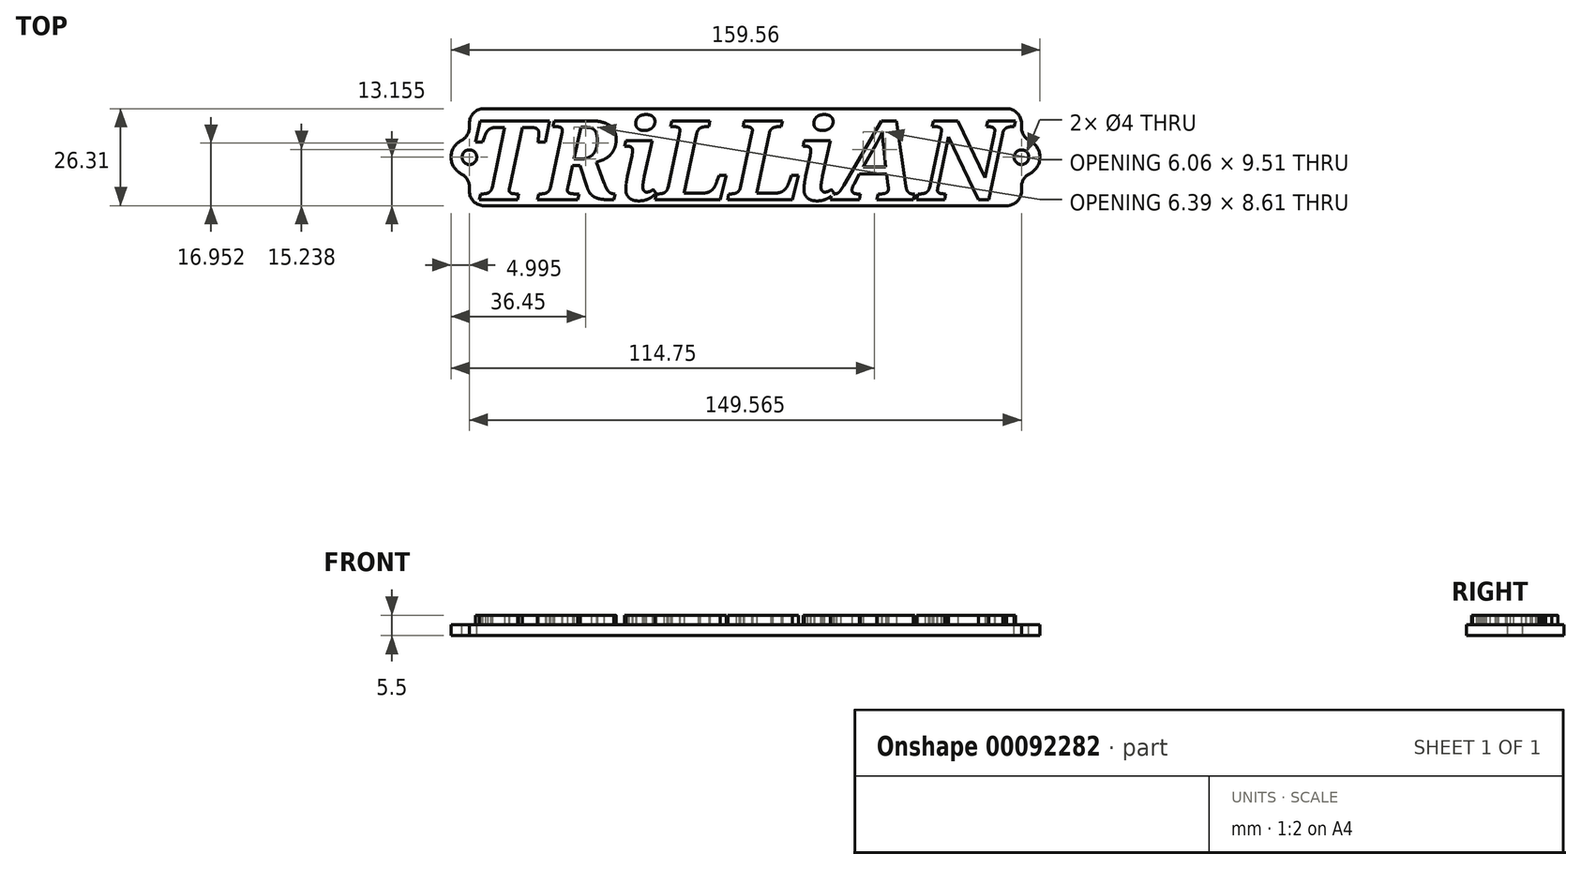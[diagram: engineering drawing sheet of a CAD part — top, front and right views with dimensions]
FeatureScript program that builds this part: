
annotation { "Feature Type Name" : "Feature", "Feature Type Description" : "" }
export const myFeature = defineFeature(function(context is Context, id is Id, definition is map)
    precondition{}
    {
        {
            var Q0;
            Q0=qCreatedBy(makeId("Top.planeOp"),FACE);
            var sketch = newSketch(context, id + "F0", { "sketchPlane" : qUnion([Q0])});
            skText(sketch, "E0", { "text": "TRiLLiAN", "fontName": "NotoSerif-BoldItalic.ttf"});
            const initialGuessF0  = {"E0": [-0.075, 0, 1, 0, 0.02161]};
            skSetInitialGuess(sketch, initialGuessF0);
            skSolve(sketch);
        }
        {
            var Q0;
            Q0=makeQuery(id+"F0.imprint","IMPRINT",FACE,{"disambiguationData":[TD([[makeQuery(id+"F0.imprint","IMPRINT",EDGE,{"derivedFrom":sQuery(id+"F0.wireOp",EDGE,"E0.sketch_text.stroke-0")}),-1.0]])]});
            var Q1;
            Q1=makeQuery(id+"F0.imprint","IMPRINT",FACE,{"disambiguationData":[TD([[makeQuery(id+"F0.imprint","IMPRINT",EDGE,{"derivedFrom":sQuery(id+"F0.wireOp",EDGE,"E0.sketch_text.stroke-91")}),-1.0]])]});
            var Q2;
            Q2=makeQuery(id+"F0.imprint","IMPRINT",FACE,{"disambiguationData":[TD([[makeQuery(id+"F0.imprint","IMPRINT",EDGE,{"derivedFrom":sQuery(id+"F0.wireOp",EDGE,"E0.sketch_text.stroke-119")}),-1.0]])]});
            var Q3;
            Q3=makeQuery(id+"F0.imprint","IMPRINT",FACE,{"disambiguationData":[TD([[makeQuery(id+"F0.imprint","IMPRINT",EDGE,{"derivedFrom":sQuery(id+"F0.wireOp",EDGE,"E0.sketch_text.stroke-135")}),-1.0]])]});
            var Q4;
            Q4=makeQuery(id+"F0.imprint","IMPRINT",FACE,{"disambiguationData":[TD([[makeQuery(id+"F0.imprint","IMPRINT",EDGE,{"derivedFrom":sQuery(id+"F0.wireOp",EDGE,"E0.sketch_text.stroke-166")}),-1.0]])]});
            var Q5;
            Q5=makeQuery(id+"F0.imprint","IMPRINT",FACE,{"disambiguationData":[TD([[makeQuery(id+"F0.imprint","IMPRINT",EDGE,{"derivedFrom":sQuery(id+"F0.wireOp",EDGE,"E0.sketch_text.stroke-225")}),-1.0]])]});
            var Q6;
            Q6=makeQuery(id+"F0.imprint","IMPRINT",FACE,{"disambiguationData":[TD([[makeQuery(id+"F0.imprint","IMPRINT",EDGE,{"derivedFrom":sQuery(id+"F0.wireOp",EDGE,"E0.sketch_text.stroke-284")}),-1.0]])]});
            var Q7;
            Q7=makeQuery(id+"F0.imprint","IMPRINT",FACE,{"disambiguationData":[TD([[makeQuery(id+"F0.imprint","IMPRINT",EDGE,{"derivedFrom":sQuery(id+"F0.wireOp",EDGE,"E0.sketch_text.stroke-35")}),-1.0]])]});
            var Q8;
            Q8=makeQuery(id+"F0.imprint","IMPRINT",FACE,{"disambiguationData":[TD([[makeQuery(id+"F0.imprint","IMPRINT",EDGE,{"derivedFrom":sQuery(id+"F0.wireOp",EDGE,"E0.sketch_text.stroke-197")}),-1.0]])]});
            var Q9;
            Q9=makeQuery(id+"F0.imprint","IMPRINT",FACE,{"disambiguationData":[TD([[makeQuery(id+"F0.imprint","IMPRINT",EDGE,{"derivedFrom":sQuery(id+"F0.wireOp",EDGE,"E0.sketch_text.stroke-241")}),-1.0]])]});
            var Q10;
            {var subQ0=sQuery(id+"F0.wireOp",EDGE,"E0.sketch_text.stroke-250");var subQ1=sQuery(id+"F0.wireOp",EDGE,"E0.sketch_text.stroke-205");var subQ2=makeQuery(id+"F0.imprint","INTERSECT",VERTEX,{"derivedFrom":[subQ1,subQ0]});Q10=makeQuery(id+"F0.imprint","IMPRINT",FACE,{"disambiguationData":[TD([[makeQuery(id+"F0.imprint","IMPRINT",EDGE,{"disambiguationData":[TD([[subQ2,-1.0]])],"derivedFrom":subQ1}),-1.0]])]});}
            var Q11;
            Q11 = qSketchRegion(id + "F0", true);
            extrude(context, id + "F1", {"entities" : qUnion([Q0, Q1, Q2, Q3, Q4, Q5, Q6, Q7, Q8, Q9, Q10, Q11]), "offsetDistance" : 25 * mm, "depth" : 2.5 * mm});
        }
        {
            var Q0;
            Q0=makeQuery(id+"F1.opExtrude","SWEPT_BODY",BODY,{"disambiguationData":[OSD([sQuery(id+"F0.wireOp",EDGE,"E0.sketch_text.stroke-284"),sQuery(id+"F0.wireOp",EDGE,"E0.sketch_text.stroke-285"),sQuery(id+"F0.wireOp",EDGE,"E0.sketch_text.stroke-286"),sQuery(id+"F0.wireOp",EDGE,"E0.sketch_text.stroke-287"),sQuery(id+"F0.wireOp",EDGE,"E0.sketch_text.stroke-288"),sQuery(id+"F0.wireOp",EDGE,"E0.sketch_text.stroke-289"),sQuery(id+"F0.wireOp",EDGE,"E0.sketch_text.stroke-290"),sQuery(id+"F0.wireOp",EDGE,"E0.sketch_text.stroke-291"),sQuery(id+"F0.wireOp",EDGE,"E0.sketch_text.stroke-292"),sQuery(id+"F0.wireOp",EDGE,"E0.sketch_text.stroke-293"),sQuery(id+"F0.wireOp",EDGE,"E0.sketch_text.stroke-294"),sQuery(id+"F0.wireOp",EDGE,"E0.sketch_text.stroke-295"),sQuery(id+"F0.wireOp",EDGE,"E0.sketch_text.stroke-296"),sQuery(id+"F0.wireOp",EDGE,"E0.sketch_text.stroke-297"),sQuery(id+"F0.wireOp",EDGE,"E0.sketch_text.stroke-298"),sQuery(id+"F0.wireOp",EDGE,"E0.sketch_text.stroke-299"),sQuery(id+"F0.wireOp",EDGE,"E0.sketch_text.stroke-300"),sQuery(id+"F0.wireOp",EDGE,"E0.sketch_text.stroke-301"),sQuery(id+"F0.wireOp",EDGE,"E0.sketch_text.stroke-302"),sQuery(id+"F0.wireOp",EDGE,"E0.sketch_text.stroke-303"),sQuery(id+"F0.wireOp",EDGE,"E0.sketch_text.stroke-304"),sQuery(id+"F0.wireOp",EDGE,"E0.sketch_text.stroke-305"),sQuery(id+"F0.wireOp",EDGE,"E0.sketch_text.stroke-306"),sQuery(id+"F0.wireOp",EDGE,"E0.sketch_text.stroke-307"),sQuery(id+"F0.wireOp",EDGE,"E0.sketch_text.stroke-308"),sQuery(id+"F0.wireOp",EDGE,"E0.sketch_text.stroke-309"),sQuery(id+"F0.wireOp",EDGE,"E0.sketch_text.stroke-310"),sQuery(id+"F0.wireOp",EDGE,"E0.sketch_text.stroke-311"),sQuery(id+"F0.wireOp",EDGE,"E0.sketch_text.stroke-312"),sQuery(id+"F0.wireOp",EDGE,"E0.sketch_text.stroke-313"),sQuery(id+"F0.wireOp",EDGE,"E0.sketch_text.stroke-314"),sQuery(id+"F0.wireOp",EDGE,"E0.sketch_text.stroke-315"),sQuery(id+"F0.wireOp",EDGE,"E0.sketch_text.stroke-316"),sQuery(id+"F0.wireOp",EDGE,"E0.sketch_text.stroke-317"),sQuery(id+"F0.wireOp",EDGE,"E0.sketch_text.stroke-318"),sQuery(id+"F0.wireOp",EDGE,"E0.sketch_text.stroke-319"),sQuery(id+"F0.wireOp",EDGE,"E0.sketch_text.stroke-320"),sQuery(id+"F0.wireOp",EDGE,"E0.sketch_text.stroke-321"),sQuery(id+"F0.wireOp",EDGE,"E0.sketch_text.stroke-322"),sQuery(id+"F0.wireOp",EDGE,"E0.sketch_text.stroke-323"),sQuery(id+"F0.wireOp",EDGE,"E0.sketch_text.stroke-324"),sQuery(id+"F0.wireOp",EDGE,"E0.sketch_text.stroke-325"),sQuery(id+"F0.wireOp",EDGE,"E0.sketch_text.stroke-326"),sQuery(id+"F0.wireOp",EDGE,"E0.sketch_text.stroke-327")])]});
            var Q1;
            Q1=makeQuery(id+"F1.opExtrude","SWEPT_BODY",BODY,{"disambiguationData":[OSD([sQuery(id+"F0.wireOp",EDGE,"E0.sketch_text.stroke-197"),sQuery(id+"F0.wireOp",EDGE,"E0.sketch_text.stroke-198"),sQuery(id+"F0.wireOp",EDGE,"E0.sketch_text.stroke-199"),sQuery(id+"F0.wireOp",EDGE,"E0.sketch_text.stroke-200"),sQuery(id+"F0.wireOp",EDGE,"E0.sketch_text.stroke-201"),sQuery(id+"F0.wireOp",EDGE,"E0.sketch_text.stroke-202"),sQuery(id+"F0.wireOp",EDGE,"E0.sketch_text.stroke-203"),sQuery(id+"F0.wireOp",EDGE,"E0.sketch_text.stroke-204"),sQuery(id+"F0.wireOp",EDGE,"E0.sketch_text.stroke-205"),sQuery(id+"F0.wireOp",EDGE,"E0.sketch_text.stroke-206"),sQuery(id+"F0.wireOp",EDGE,"E0.sketch_text.stroke-207"),sQuery(id+"F0.wireOp",EDGE,"E0.sketch_text.stroke-208"),sQuery(id+"F0.wireOp",EDGE,"E0.sketch_text.stroke-209"),sQuery(id+"F0.wireOp",EDGE,"E0.sketch_text.stroke-210"),sQuery(id+"F0.wireOp",EDGE,"E0.sketch_text.stroke-211"),sQuery(id+"F0.wireOp",EDGE,"E0.sketch_text.stroke-212"),sQuery(id+"F0.wireOp",EDGE,"E0.sketch_text.stroke-213"),sQuery(id+"F0.wireOp",EDGE,"E0.sketch_text.stroke-214"),sQuery(id+"F0.wireOp",EDGE,"E0.sketch_text.stroke-215"),sQuery(id+"F0.wireOp",EDGE,"E0.sketch_text.stroke-216"),sQuery(id+"F0.wireOp",EDGE,"E0.sketch_text.stroke-217"),sQuery(id+"F0.wireOp",EDGE,"E0.sketch_text.stroke-218"),sQuery(id+"F0.wireOp",EDGE,"E0.sketch_text.stroke-219"),sQuery(id+"F0.wireOp",EDGE,"E0.sketch_text.stroke-220"),sQuery(id+"F0.wireOp",EDGE,"E0.sketch_text.stroke-221"),sQuery(id+"F0.wireOp",EDGE,"E0.sketch_text.stroke-222"),sQuery(id+"F0.wireOp",EDGE,"E0.sketch_text.stroke-223"),sQuery(id+"F0.wireOp",EDGE,"E0.sketch_text.stroke-224"),sQuery(id+"F0.wireOp",EDGE,"E0.sketch_text.stroke-241"),sQuery(id+"F0.wireOp",EDGE,"E0.sketch_text.stroke-242"),sQuery(id+"F0.wireOp",EDGE,"E0.sketch_text.stroke-243"),sQuery(id+"F0.wireOp",EDGE,"E0.sketch_text.stroke-244"),sQuery(id+"F0.wireOp",EDGE,"E0.sketch_text.stroke-245"),sQuery(id+"F0.wireOp",EDGE,"E0.sketch_text.stroke-246"),sQuery(id+"F0.wireOp",EDGE,"E0.sketch_text.stroke-247"),sQuery(id+"F0.wireOp",EDGE,"E0.sketch_text.stroke-248"),sQuery(id+"F0.wireOp",EDGE,"E0.sketch_text.stroke-249"),sQuery(id+"F0.wireOp",EDGE,"E0.sketch_text.stroke-250"),sQuery(id+"F0.wireOp",EDGE,"E0.sketch_text.stroke-251"),sQuery(id+"F0.wireOp",EDGE,"E0.sketch_text.stroke-252"),sQuery(id+"F0.wireOp",EDGE,"E0.sketch_text.stroke-253"),sQuery(id+"F0.wireOp",EDGE,"E0.sketch_text.stroke-254"),sQuery(id+"F0.wireOp",EDGE,"E0.sketch_text.stroke-255"),sQuery(id+"F0.wireOp",EDGE,"E0.sketch_text.stroke-256"),sQuery(id+"F0.wireOp",EDGE,"E0.sketch_text.stroke-257"),sQuery(id+"F0.wireOp",EDGE,"E0.sketch_text.stroke-258"),sQuery(id+"F0.wireOp",EDGE,"E0.sketch_text.stroke-259"),sQuery(id+"F0.wireOp",EDGE,"E0.sketch_text.stroke-260"),sQuery(id+"F0.wireOp",EDGE,"E0.sketch_text.stroke-261"),sQuery(id+"F0.wireOp",EDGE,"E0.sketch_text.stroke-262"),sQuery(id+"F0.wireOp",EDGE,"E0.sketch_text.stroke-263"),sQuery(id+"F0.wireOp",EDGE,"E0.sketch_text.stroke-264"),sQuery(id+"F0.wireOp",EDGE,"E0.sketch_text.stroke-265"),sQuery(id+"F0.wireOp",EDGE,"E0.sketch_text.stroke-266"),sQuery(id+"F0.wireOp",EDGE,"E0.sketch_text.stroke-267"),sQuery(id+"F0.wireOp",EDGE,"E0.sketch_text.stroke-268"),sQuery(id+"F0.wireOp",EDGE,"E0.sketch_text.stroke-269"),sQuery(id+"F0.wireOp",EDGE,"E0.sketch_text.stroke-270"),sQuery(id+"F0.wireOp",EDGE,"E0.sketch_text.stroke-271"),sQuery(id+"F0.wireOp",EDGE,"E0.sketch_text.stroke-272"),sQuery(id+"F0.wireOp",EDGE,"E0.sketch_text.stroke-273"),sQuery(id+"F0.wireOp",EDGE,"E0.sketch_text.stroke-274"),sQuery(id+"F0.wireOp",EDGE,"E0.sketch_text.stroke-275"),sQuery(id+"F0.wireOp",EDGE,"E0.sketch_text.stroke-276"),sQuery(id+"F0.wireOp",EDGE,"E0.sketch_text.stroke-277"),sQuery(id+"F0.wireOp",EDGE,"E0.sketch_text.stroke-278"),sQuery(id+"F0.wireOp",EDGE,"E0.sketch_text.stroke-279"),sQuery(id+"F0.wireOp",EDGE,"E0.sketch_text.stroke-280"),sQuery(id+"F0.wireOp",EDGE,"E0.sketch_text.stroke-281"),sQuery(id+"F0.wireOp",EDGE,"E0.sketch_text.stroke-282"),sQuery(id+"F0.wireOp",EDGE,"E0.sketch_text.stroke-283")])]});
            var Q2;
            Q2=makeQuery(id+"F1.opExtrude","SWEPT_BODY",BODY,{"disambiguationData":[OSD([sQuery(id+"F0.wireOp",EDGE,"E0.sketch_text.stroke-225"),sQuery(id+"F0.wireOp",EDGE,"E0.sketch_text.stroke-226"),sQuery(id+"F0.wireOp",EDGE,"E0.sketch_text.stroke-227"),sQuery(id+"F0.wireOp",EDGE,"E0.sketch_text.stroke-228"),sQuery(id+"F0.wireOp",EDGE,"E0.sketch_text.stroke-229"),sQuery(id+"F0.wireOp",EDGE,"E0.sketch_text.stroke-230"),sQuery(id+"F0.wireOp",EDGE,"E0.sketch_text.stroke-231"),sQuery(id+"F0.wireOp",EDGE,"E0.sketch_text.stroke-232"),sQuery(id+"F0.wireOp",EDGE,"E0.sketch_text.stroke-233"),sQuery(id+"F0.wireOp",EDGE,"E0.sketch_text.stroke-234"),sQuery(id+"F0.wireOp",EDGE,"E0.sketch_text.stroke-235"),sQuery(id+"F0.wireOp",EDGE,"E0.sketch_text.stroke-236"),sQuery(id+"F0.wireOp",EDGE,"E0.sketch_text.stroke-237"),sQuery(id+"F0.wireOp",EDGE,"E0.sketch_text.stroke-238"),sQuery(id+"F0.wireOp",EDGE,"E0.sketch_text.stroke-239"),sQuery(id+"F0.wireOp",EDGE,"E0.sketch_text.stroke-240")])]});
            transform(context, id + "F2", {"entities" : qUnion([Q0, Q1, Q2]), "transformType" : TransformType.TRANSLATION_3D, "dx" : -1.6 * mm, "dy" : 0 * mm, "dz" : 0 * mm, "makeCopy" : false});
        }
        {
            var Q0;
            Q0=qCreatedBy(makeId("Top.planeOp"),FACE);
            var sketch = newSketch(context, id + "F3", { "sketchPlane" : qUnion([Q0])});
            skLineSegment(sketch, "E1.bottom", {"start": v(-74.56, 24.71) * mm, "end": v(75, 24.71) * mm});
            skLineSegment(sketch, "E1.top", {"start": v(-74.56, -1.6) * mm, "end": v(75, -1.6) * mm});
            skLineSegment(sketch, "E1.left", {"start": v(-74.56, 24.71) * mm, "end": v(-74.56, -1.6) * mm});
            skLineSegment(sketch, "E1.right", {"start": v(75, 24.71) * mm, "end": v(75, -1.6) * mm});
            skCircle(sketch, "E2", {"center": v(-74.56, 11.56) * mm, "radius": 2 * mm});
            skCircle(sketch, "E3", {"center": v(-74.56, 11.56) * mm, "radius": 5 * mm});
            skCircle(sketch, "E4", {"center": v(75, 11.56) * mm, "radius": 2 * mm});
            skCircle(sketch, "E5", {"center": v(75, 11.56) * mm, "radius": 5 * mm});
            skSolve(sketch);
        }
        {
            var Q0;
            {var subQ1=sQuery(id+"F3.wireOp",EDGE,"E1.bottom");Q0=makeQuery(id+"F3.imprint","IMPRINT",FACE,{"disambiguationData":[TD([[makeQuery(id+"F3.imprint","IMPRINT",EDGE,{"derivedFrom":subQ1}),-1.0]])]});}
            var Q1;
            {var subQ0=sQuery(id+"F3.wireOp",EDGE,"E3");var subQ1=sQuery(id+"F3.wireOp",EDGE,"E1.left");var subQ2=makeQuery(id+"F3.imprint","INTERSECT",VERTEX,{"disambiguationData":[OD(1.0)],"derivedFrom":[subQ1,subQ0]});Q1=makeQuery(id+"F3.imprint","IMPRINT",FACE,{"disambiguationData":[TD([[makeQuery(id+"F3.imprint","IMPRINT",EDGE,{"disambiguationData":[TD([[subQ2,-1.0]])],"derivedFrom":subQ1}),1.0]])]});}
            var Q2;
            {var subQ0=sQuery(id+"F3.wireOp",EDGE,"E3");var subQ1=sQuery(id+"F3.wireOp",EDGE,"E1.left");var subQ2=makeQuery(id+"F3.imprint","INTERSECT",VERTEX,{"disambiguationData":[OD(1.0)],"derivedFrom":[subQ1,subQ0]});Q2=makeQuery(id+"F3.imprint","IMPRINT",FACE,{"disambiguationData":[TD([[makeQuery(id+"F3.imprint","IMPRINT",EDGE,{"disambiguationData":[TD([[subQ2,-1.0]])],"derivedFrom":subQ1}),-1.0]])]});}
            var Q3;
            {var subQ0=sQuery(id+"F3.wireOp",EDGE,"E5");var subQ1=sQuery(id+"F3.wireOp",EDGE,"E1.right");var subQ2=makeQuery(id+"F3.imprint","INTERSECT",VERTEX,{"disambiguationData":[OD(1.0)],"derivedFrom":[subQ1,subQ0]});Q3=makeQuery(id+"F3.imprint","IMPRINT",FACE,{"disambiguationData":[TD([[makeQuery(id+"F3.imprint","IMPRINT",EDGE,{"disambiguationData":[TD([[subQ2,-1.0]])],"derivedFrom":subQ1}),-1.0]])]});}
            var Q4;
            {var subQ0=sQuery(id+"F3.wireOp",EDGE,"E5");var subQ1=sQuery(id+"F3.wireOp",EDGE,"E1.right");var subQ2=makeQuery(id+"F3.imprint","INTERSECT",VERTEX,{"disambiguationData":[OD(1.0)],"derivedFrom":[subQ1,subQ0]});Q4=makeQuery(id+"F3.imprint","IMPRINT",FACE,{"disambiguationData":[TD([[makeQuery(id+"F3.imprint","IMPRINT",EDGE,{"disambiguationData":[TD([[subQ2,-1.0]])],"derivedFrom":subQ1}),1.0]])]});}
            extrude(context, id + "F4", {"entities" : qUnion([Q0, Q1, Q2, Q3, Q4]), "oppositeDirection" : true, "depth" : 3 * mm, "offsetDistance" : 25 * mm});
        }
        {
            var Q0;
            Q0=makeQuery(id+"F4.opExtrude","SWEPT_EDGE",EDGE,{"disambiguationData":[OSD([sQuery(id+"F3.wireOp",EDGE,"E1.bottom"),sQuery(id+"F3.wireOp",EDGE,"E1.left")])]});
            var Q1;
            Q1=makeQuery(id+"F4.opExtrude","SWEPT_EDGE",EDGE,{"disambiguationData":[OSD([sQuery(id+"F3.wireOp",EDGE,"E1.bottom"),sQuery(id+"F3.wireOp",EDGE,"E1.right")])]});
            var Q2;
            Q2=makeQuery(id+"F4.opExtrude","SWEPT_EDGE",EDGE,{"disambiguationData":[OSD([sQuery(id+"F3.wireOp",EDGE,"E1.top"),sQuery(id+"F3.wireOp",EDGE,"E1.left")])]});
            var Q3;
            Q3=makeQuery(id+"F4.opExtrude","SWEPT_EDGE",EDGE,{"disambiguationData":[OSD([sQuery(id+"F3.wireOp",EDGE,"E1.top"),sQuery(id+"F3.wireOp",EDGE,"E1.right")])]});
            var Q4;
            {var subQ0=sQuery(id+"F3.wireOp",EDGE,"E3");var subQ1=sQuery(id+"F3.wireOp",EDGE,"E1.left");Q4=makeQuery(id+"F4.opExtrude","SWEPT_EDGE",EDGE,{"disambiguationData":[OSD([subQ1,subQ0]),TDD([makeQuery(id+"F3.imprint","INTERSECT",VERTEX,{"disambiguationData":[OD(0.0)],"derivedFrom":[subQ1,subQ0]})])]});}
            var Q5;
            {var subQ0=sQuery(id+"F3.wireOp",EDGE,"E5");var subQ1=sQuery(id+"F3.wireOp",EDGE,"E1.right");Q5=makeQuery(id+"F4.opExtrude","SWEPT_EDGE",EDGE,{"disambiguationData":[OSD([subQ1,subQ0]),TDD([makeQuery(id+"F3.imprint","INTERSECT",VERTEX,{"disambiguationData":[OD(0.0)],"derivedFrom":[subQ1,subQ0]})])]});}
            var Q6;
            {var subQ0=sQuery(id+"F3.wireOp",EDGE,"E3");var subQ1=sQuery(id+"F3.wireOp",EDGE,"E1.left");Q6=makeQuery(id+"F4.opExtrude","SWEPT_EDGE",EDGE,{"disambiguationData":[OSD([subQ1,subQ0]),TDD([makeQuery(id+"F3.imprint","INTERSECT",VERTEX,{"disambiguationData":[OD(1.0)],"derivedFrom":[subQ1,subQ0]})])]});}
            var Q7;
            {var subQ0=sQuery(id+"F3.wireOp",EDGE,"E5");var subQ1=sQuery(id+"F3.wireOp",EDGE,"E1.right");Q7=makeQuery(id+"F4.opExtrude","SWEPT_EDGE",EDGE,{"disambiguationData":[OSD([subQ1,subQ0]),TDD([makeQuery(id+"F3.imprint","INTERSECT",VERTEX,{"disambiguationData":[OD(1.0)],"derivedFrom":[subQ1,subQ0]})])]});}
            fillet(context, id + "F5", {"entities" : qUnion([Q0, Q1, Q2, Q3, Q4, Q5, Q6, Q7]), "tangentPropagation" : true, "radius" : 4 * mm, "defaultsChanged" : true, "vertexSettings" : [], "allowEdgeOverflow" : false});
        }
    });
